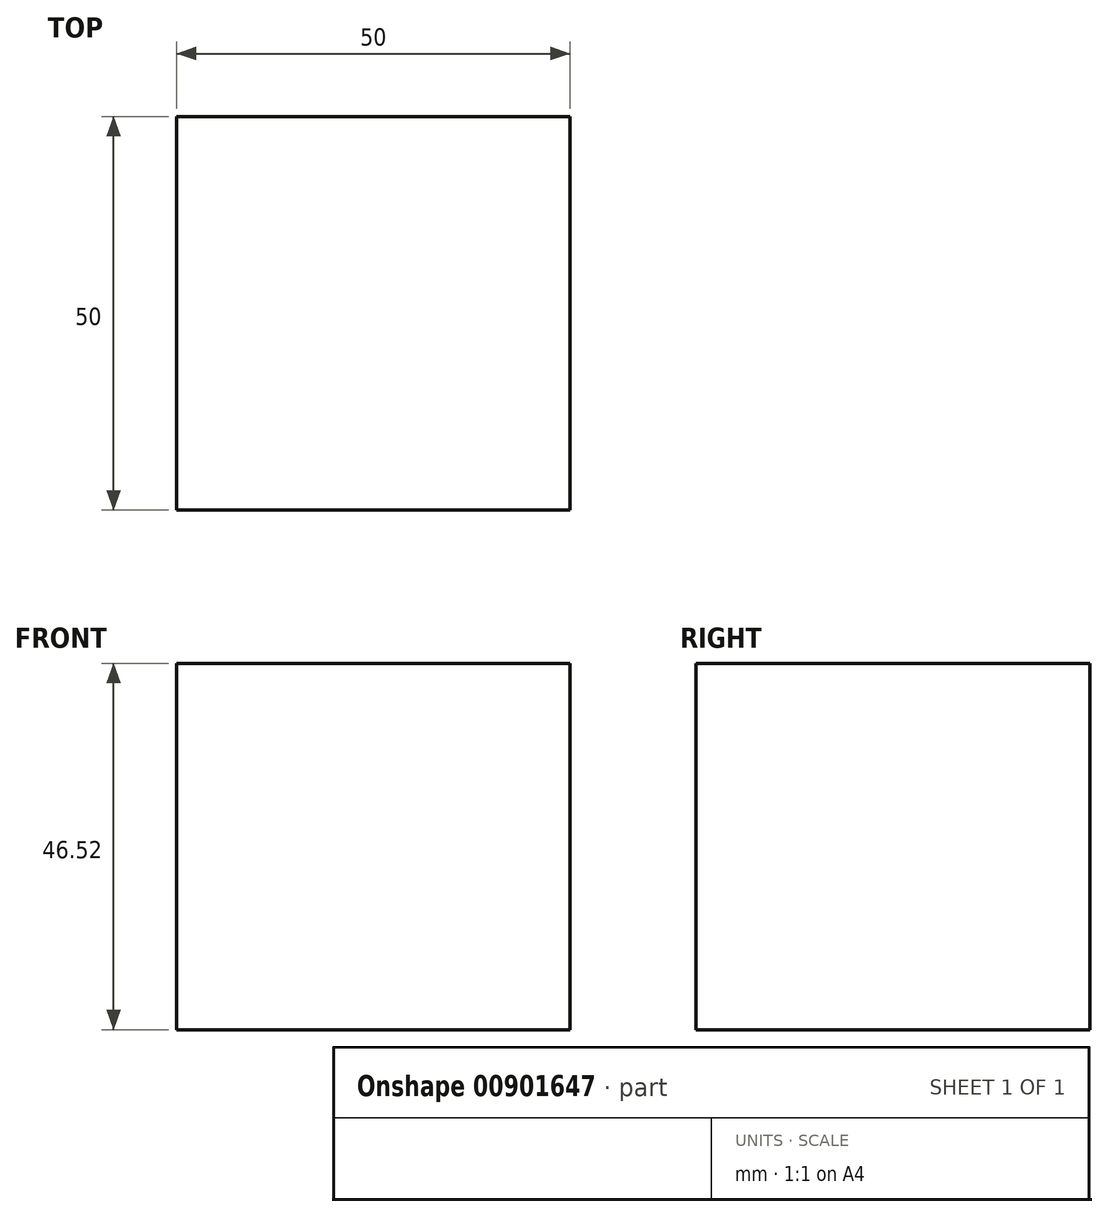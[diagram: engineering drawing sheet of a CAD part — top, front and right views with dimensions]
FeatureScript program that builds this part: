
annotation { "Feature Type Name" : "Feature", "Feature Type Description" : "" }
export const myFeature = defineFeature(function(context is Context, id is Id, definition is map)
    precondition{}
    {
        {
            var Q0;
            Q0=qCreatedBy(makeId("Front.planeOp"),FACE);
            var sketch = newSketch(context, id + "F0", { "sketchPlane" : qUnion([Q0])});
            skLineSegment(sketch, "E0.bottom", {"start": v(25, 23.26) * mm, "end": v(-25, 23.26) * mm});
            skLineSegment(sketch, "E0.top", {"start": v(25, -23.26) * mm, "end": v(-25, -23.26) * mm});
            skLineSegment(sketch, "E0.left", {"start": v(25, 23.26) * mm, "end": v(25, -23.26) * mm});
            skLineSegment(sketch, "E0.right", {"start": v(-25, 23.26) * mm, "end": v(-25, -23.26) * mm});
            skPoint(sketch, "E0.middle", {"position": v(0, 0) * mm});
            skSolve(sketch);
        }
        {
            var Q0;
            Q0 = qSketchRegion(id + "F0", true);
            extrude(context, id + "F1", {"entities" : qUnion([Q0]), "endBound" : BoundingType.SYMMETRIC, "depth" : 50 * mm, "offsetDistance" : 25 * mm});
        }
    });
